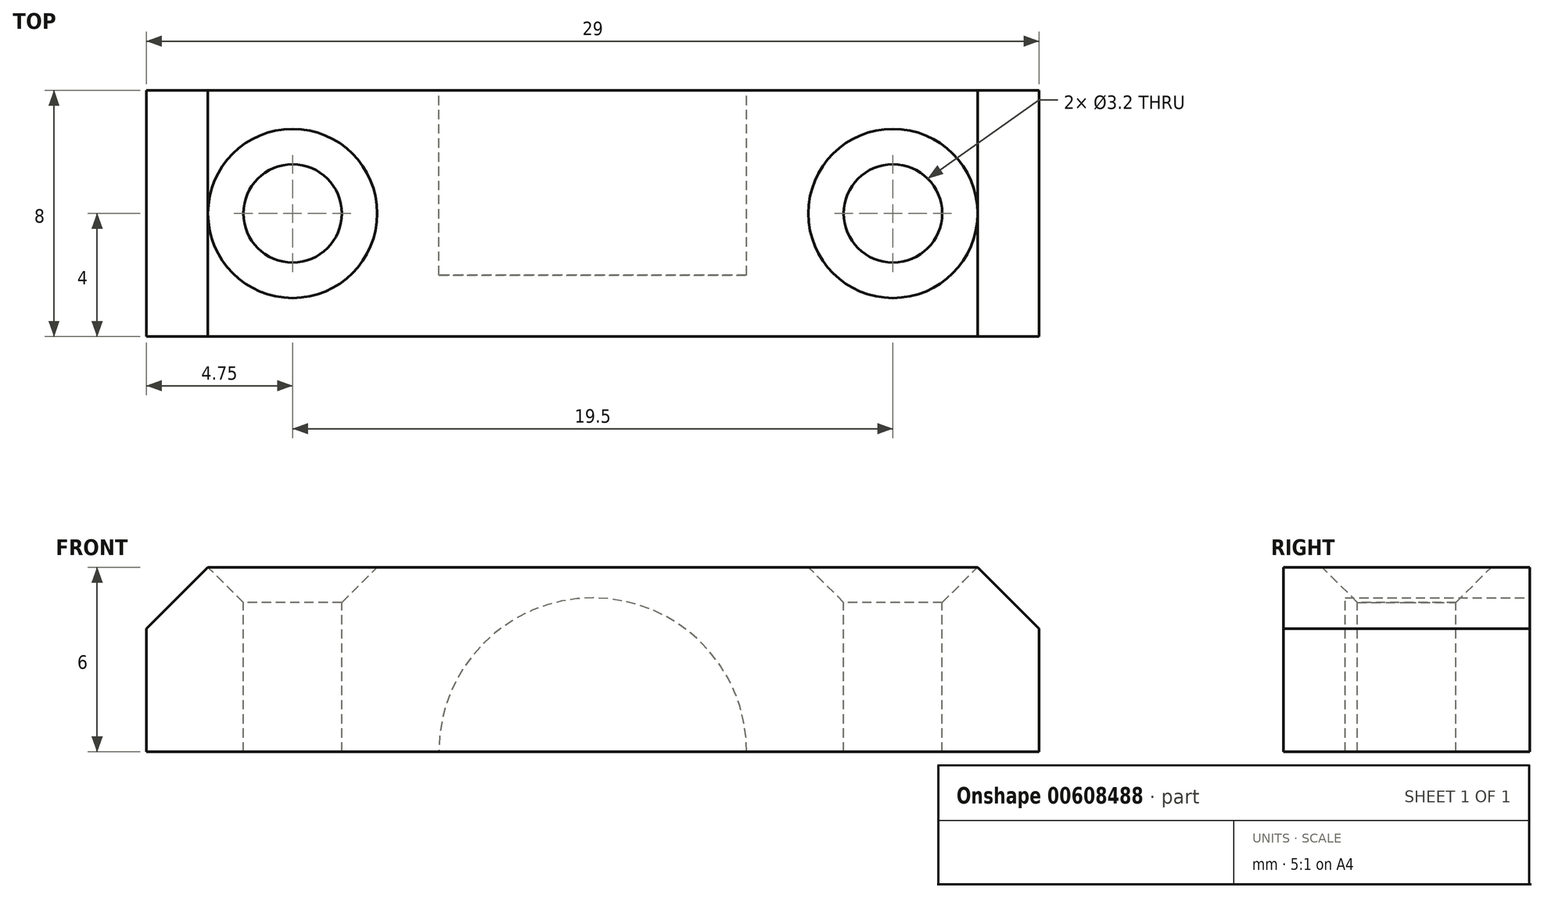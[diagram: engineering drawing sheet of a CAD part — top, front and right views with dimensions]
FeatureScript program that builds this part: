
annotation { "Feature Type Name" : "Feature", "Feature Type Description" : "" }
export const myFeature = defineFeature(function(context is Context, id is Id, definition is map)
    precondition{}
    {
        {
            var Q0;
            Q0=qCreatedBy(makeId("Front.planeOp"),FACE);
            var sketch = newSketch(context, id + "F0", { "sketchPlane" : qUnion([Q0])});
            skLineSegment(sketch, "E0.bottom", {"start": v(0, 0) * mm, "end": v(29, 0) * mm});
            skLineSegment(sketch, "E0.top", {"start": v(0, 6) * mm, "end": v(29, 6) * mm});
            skLineSegment(sketch, "E0.left", {"start": v(0, 0) * mm, "end": v(0, 6) * mm});
            skLineSegment(sketch, "E0.right", {"start": v(29, 0) * mm, "end": v(29, 6) * mm});
            skSolve(sketch);
        }
        {
            var Q0;
            Q0 = qSketchRegion(id + "F0", true);
            extrude(context, id + "F1", {"entities" : qUnion([Q0]), "depth" : 8 * mm, "offsetDistance" : 25 * mm});
        }
        {
            var Q0;
            Q0=makeQuery(id+"F1.opExtrude","CAP_FACE",FACE,{"disambiguationData":[OSD([sQuery(id+"F0.wireOp",EDGE,"E0.bottom"),sQuery(id+"F0.wireOp",EDGE,"E0.top"),sQuery(id+"F0.wireOp",EDGE,"E0.left"),sQuery(id+"F0.wireOp",EDGE,"E0.right")])],"isStart":true});
            var sketch = newSketch(context, id + "F2", { "sketchPlane" : qUnion([Q0])});
            skPoint(sketch, "E1", {"position": v(-14.5, 0) * mm});
            skCircle(sketch, "E2", {"center": v(-14.5, 0) * mm, "radius": 5 * mm});
            skSolve(sketch);
        }
        {
            var Q0;
            Q0 = qSketchRegion(id + "F2", true);
            extrude(context, id + "F3", {"entities" : qUnion([Q0]), "operationType" : NewBodyOperationType.REMOVE, "oppositeDirection" : true, "depth" : 6 * mm, "offsetDistance" : 25 * mm});
        }
        {
            var Q0;
            Q0=makeQuery(id+"F1.opExtrude","SWEPT_FACE",FACE,{"disambiguationData":[OSD([sQuery(id+"F0.wireOp",EDGE,"E0.top")])]});
            var sketch = newSketch(context, id + "F4", { "sketchPlane" : qUnion([Q0])});
            skPoint(sketch, "E3", {"position": v(29, -4) * mm});
            skPoint(sketch, "E4", {"position": v(0, -4) * mm});
            skPoint(sketch, "E5", {"position": v(14.5, -8) * mm});
            skLineSegment(sketch, "E6", {"start": v(14.5, -8) * mm, "end": v(14.5, -4) * mm, "construction": true});
            skCircle(sketch, "E7", {"center": v(14.5, -4) * mm, "radius": 5 * mm, "construction": true});
            skLineSegment(sketch, "E8", {"start": v(29, -4) * mm, "end": v(19.5, -4) * mm, "construction": true});
            skLineSegment(sketch, "E9", {"start": v(0, -4) * mm, "end": v(9.5, -4) * mm, "construction": true});
            skPoint(sketch, "E10", {"position": v(24.25, -4) * mm});
            skPoint(sketch, "E11", {"position": v(4.75, -4) * mm});
            skCircle(sketch, "E12", {"center": v(4.75, -4) * mm, "radius": 2.75 * mm});
            skCircle(sketch, "E13", {"center": v(24.25, -4) * mm, "radius": 2.75 * mm});
            skSolve(sketch);
        }
        {
            var Q0;
            Q0=sQuery(id+"F4.wireOp",VERTEX,"E11");
            var Q1;
            Q1=sQuery(id+"F4.wireOp",VERTEX,"E13.center");
            var Q2;
            Q2=makeQuery(id+"F1.opExtrude","SWEPT_BODY",BODY,{"disambiguationData":[OSD([sQuery(id+"F0.wireOp",EDGE,"E0.bottom"),sQuery(id+"F0.wireOp",EDGE,"E0.top"),sQuery(id+"F0.wireOp",EDGE,"E0.left"),sQuery(id+"F0.wireOp",EDGE,"E0.right")])]});
            hole(context, id + "F5", {"style" : HoleStyle.C_SINK, "endStyle" : HoleEndStyle.BLIND, "holeDiameter" : 3.2 * mm, "cSinkDiameter" : 5.5 * mm, "cSinkAngle" : 90 * degree, "majorDiameter" : 5 * mm, "holeDepth" : 10 * mm, "isTappedThrough" : true, "tappedDepth" : 12 * mm, "tapClearance" : 3, "startFromSketch" : true, "locations" : qUnion([Q0, Q1]), "scope" : qUnion([Q2])});
        }
        {
            var Q0;
            Q0=makeQuery(id+"F1.opExtrude","SWEPT_EDGE",EDGE,{"disambiguationData":[OSD([sQuery(id+"F0.wireOp",EDGE,"E0.top"),sQuery(id+"F0.wireOp",EDGE,"E0.right")])]});
            var Q1;
            Q1=makeQuery(id+"F1.opExtrude","SWEPT_EDGE",EDGE,{"disambiguationData":[OSD([sQuery(id+"F0.wireOp",EDGE,"E0.top"),sQuery(id+"F0.wireOp",EDGE,"E0.left")])]});
            chamfer(context, id + "F6", {"entities" : qUnion([Q0, Q1]), "width" : 2 * mm, "tangentPropagation" : true});
        }
    });
